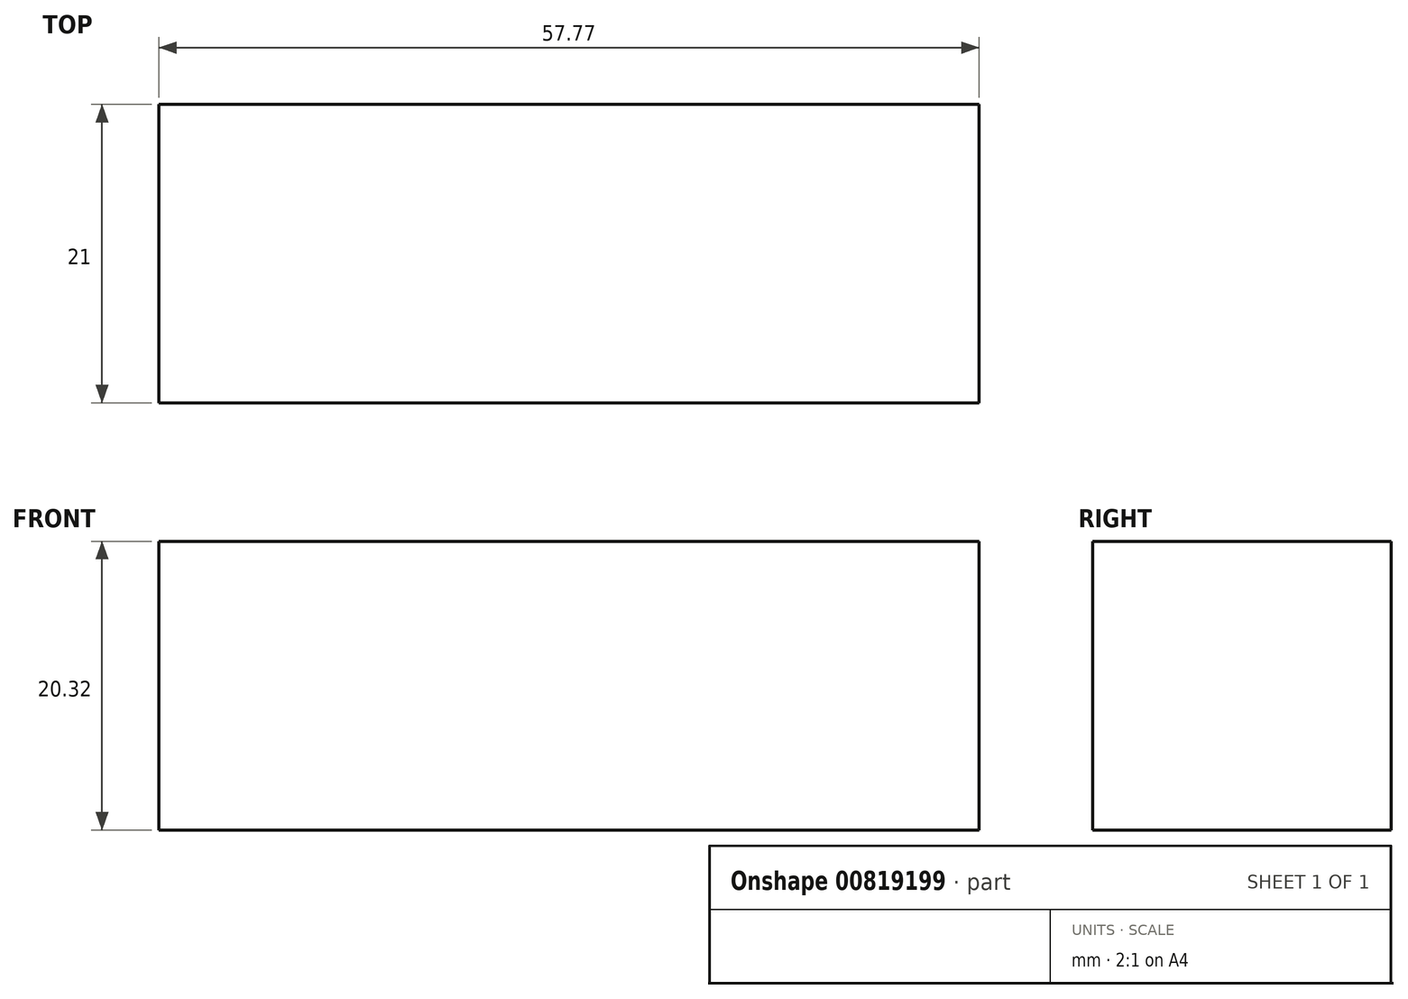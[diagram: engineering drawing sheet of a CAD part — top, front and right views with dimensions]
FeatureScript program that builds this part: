
annotation { "Feature Type Name" : "Feature", "Feature Type Description" : "" }
export const myFeature = defineFeature(function(context is Context, id is Id, definition is map)
    precondition{}
    {
        {
            var Q0;
            Q0=qCreatedBy(makeId("Top.planeOp"),FACE);
            var sketch = newSketch(context, id + "F0", { "sketchPlane" : qUnion([Q0])});
            skLineSegment(sketch, "E0.bottom", {"start": v(-93.17, 0) * mm, "end": v(-35.4, 0) * mm});
            skLineSegment(sketch, "E0.top", {"start": v(-93.17, 21) * mm, "end": v(-35.4, 21) * mm});
            skLineSegment(sketch, "E0.left", {"start": v(-93.17, 0) * mm, "end": v(-93.17, 21) * mm});
            skLineSegment(sketch, "E0.right", {"start": v(-35.4, 0) * mm, "end": v(-35.4, 21) * mm});
            skSolve(sketch);
        }
        {
            var Q0;
            Q0 = qSketchRegion(id + "F0", true);
            extrude(context, id + "F1", {"entities" : qUnion([Q0]), "depth" : 20.32 * mm, "offsetDistance" : 25.4 * mm});
        }
    });
